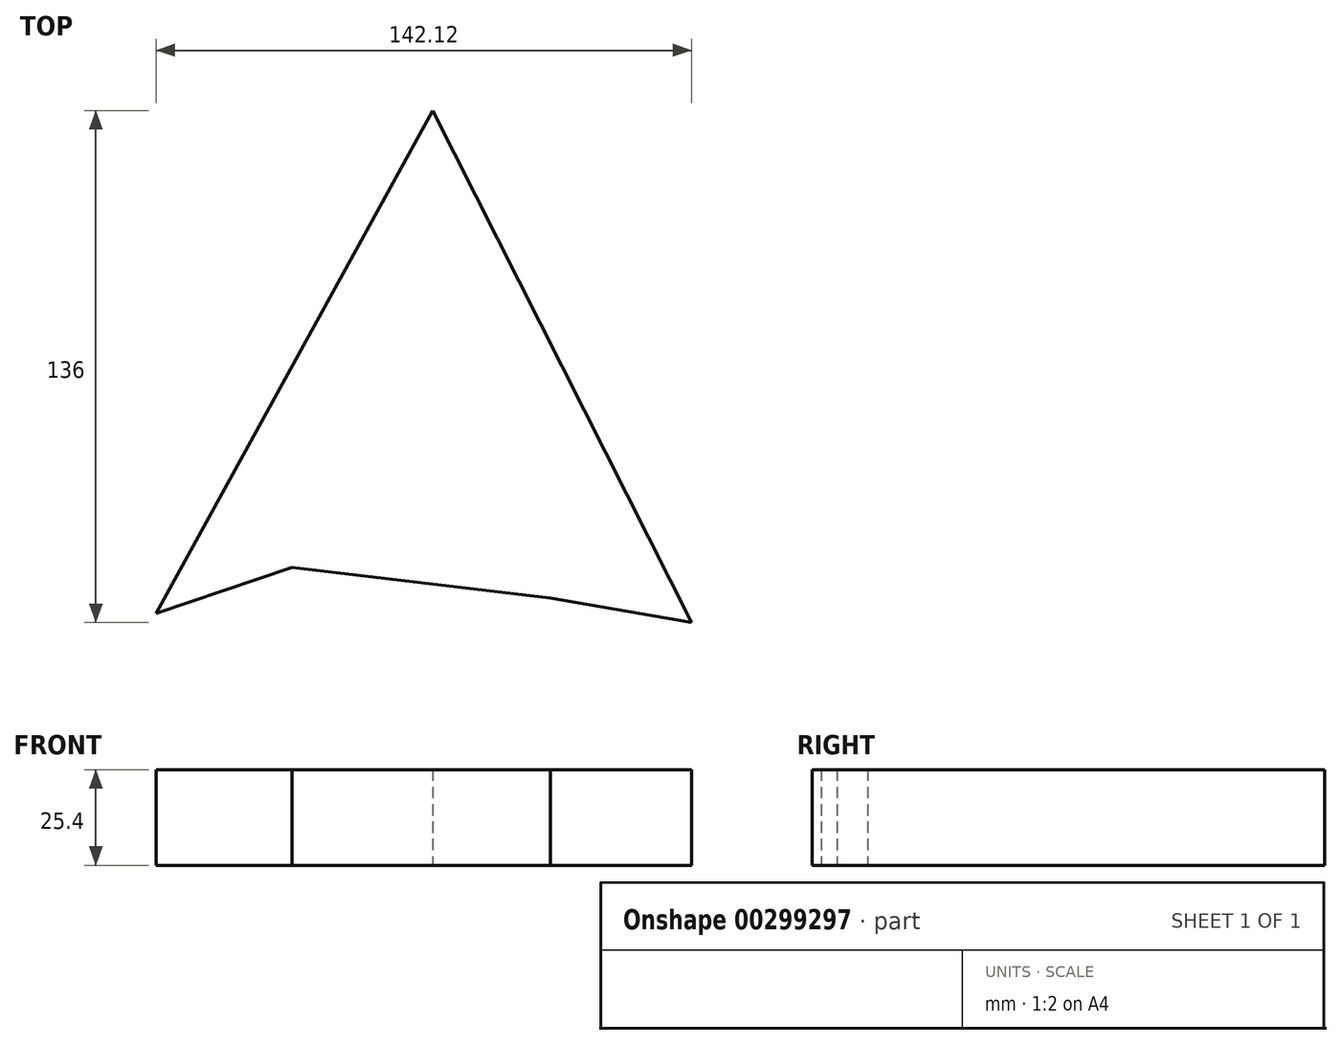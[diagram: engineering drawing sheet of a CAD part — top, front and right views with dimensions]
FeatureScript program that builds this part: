
annotation { "Feature Type Name" : "Feature", "Feature Type Description" : "" }
export const myFeature = defineFeature(function(context is Context, id is Id, definition is map)
    precondition{}
    {
        {
            var Q0;
            Q0=qCreatedBy(makeId("Top.planeOp"),FACE);
            var sketch = newSketch(context, id + "F0", { "sketchPlane" : qUnion([Q0])});
            skLineSegment(sketch, "E0", {"start": v(12.95, 21.87) * mm, "end": v(12.95, -34.54) * mm});
            skLineSegment(sketch, "E1", {"start": v(12.95, 21.87) * mm, "end": v(33.67, -35.69) * mm});
            skLineSegment(sketch, "E2", {"start": v(33.67, -35.69) * mm, "end": v(12.95, -34.54) * mm});
            skLineSegment(sketch, "E3", {"start": v(4.6, 44.9) * mm, "end": v(4.6, -54.68) * mm, "construction": true});
            skSolve(sketch);
        }
        {
            var Q0;
            Q0 = qSketchRegion(id + "F0", true);
            var Q1;
            Q1 = qConstructionFilter(qBodyType(qCreatedBy(id + "F0" ,EDGE), BodyType.WIRE), ConstructionObject.NO);
            var Q2;
            Q2=sQuery(id+"F0.wireOp",EDGE,"E3");
            revolve(context, id + "F1", {"bodyType" : ToolBodyType.SURFACE, "entities" : qUnion([Q0]), "surfaceEntities" : qUnion([Q1]), "axis" : qUnion([Q2]), "revolveType" : RevolveType.FULL});
        }
        {
            var Q0;
            Q0=qCreatedBy(makeId("Top.planeOp"),FACE);
            var sketch = newSketch(context, id + "F2", { "sketchPlane" : qUnion([Q0])});
            skLineSegment(sketch, "E4", {"start": v(31.04, 71.87) * mm, "end": v(31.04, 142.78) * mm});
            skLineSegment(sketch, "E5", {"start": v(31.04, 142.78) * mm, "end": v(-42.31, 9.2) * mm});
            skLineSegment(sketch, "E6", {"start": v(-42.31, 9.2) * mm, "end": v(-6.26, 21.5) * mm});
            skLineSegment(sketch, "E7", {"start": v(31.04, 142.78) * mm, "end": v(99.81, 6.78) * mm});
            skLineSegment(sketch, "E8", {"start": v(99.81, 6.78) * mm, "end": v(62.29, 13.37) * mm});
            skLineSegment(sketch, "E9", {"start": v(-6.26, 21.5) * mm, "end": v(62.29, 13.37) * mm});
            skLineSegment(sketch, "E10", {"start": v(-24.46, -35.69) * mm, "end": v(-3.74, 21.87) * mm});
            skLineSegment(sketch, "E11", {"start": v(12.95, 21.87) * mm, "end": v(33.67, -35.69) * mm});
            skSolve(sketch);
        }
        {
            var Q0;
            Q0 = qSketchRegion(id + "F2", true);
            extrude(context, id + "F3", {"entities" : qUnion([Q0]), "endBound" : BoundingType.SYMMETRIC, "depth" : 25.4 * mm});
        }
    });
